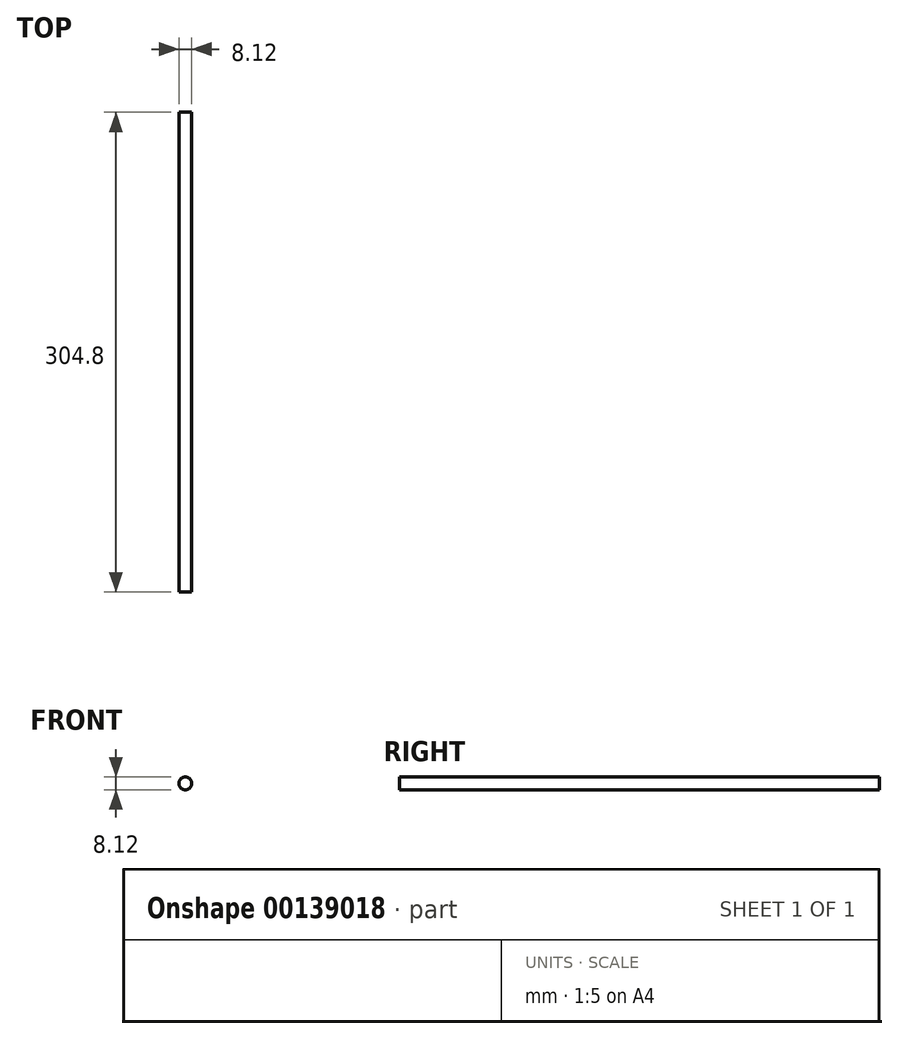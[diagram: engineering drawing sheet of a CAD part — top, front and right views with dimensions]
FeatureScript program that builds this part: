
annotation { "Feature Type Name" : "Feature", "Feature Type Description" : "" }
export const myFeature = defineFeature(function(context is Context, id is Id, definition is map)
    precondition{}
    {
        {
            var Q0;
            Q0=qCreatedBy(makeId("Front.planeOp"),FACE);
            var sketch = newSketch(context, id + "F0", { "sketchPlane" : qUnion([Q0])});
            skCircle(sketch, "E0", {"center": v(0, 0) * mm, "radius": 4.06 * mm});
            skSolve(sketch);
        }
        {
            var Q0;
            Q0 = qSketchRegion(id + "F0", true);
            extrude(context, id + "F1", {"entities" : qUnion([Q0]), "depth" : 304.8 * mm});
        }
    });
